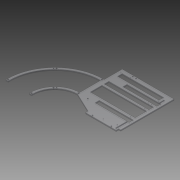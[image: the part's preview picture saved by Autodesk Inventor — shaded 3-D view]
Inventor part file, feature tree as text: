
AUTODESK INVENTOR PART (.ipt)
format: ipt  version: 2014 SP1 (Build 180222100, 222)  size: 401,920 bytes
history: native  units: in
note: dims shown in document units (in); Inventor stores cm internally (conversion verified against a paired STEP export)
features: extrude x18, sketch x18, reference x7
ambient origin geometry x8: Origin, YZ Plane, XZ Plane, XY Plane, X Axis, Y Axis, Z Axis, Center Point
bodies: Body1 (feature_tree)
feature tree (43):
  extrude  "Extrusion7"  Depth=1.0in
  extrude  "Extrusion8"  Depth=0.5in
  extrude  "Extrusion9"  Depth=5.25in
  extrude  "Extrusion10"  Depth=0.25in
  extrude  "Extrusion11"  Depth=7.625in
  extrude  "Extrusion13"  Depth=5.5in
  extrude  "Extrusion15"  Depth=12.125in
  extrude  "Extrusion16"  Depth=8.0in
  extrude  "Extrusion17"  Depth=2.75in
  extrude  "Extrusion18"  TaperAngle=90.0deg  [1 undecoded]
  extrude  "Extrusion19"  Depth=0.75in
  extrude  "Extrusion20"  Depth=10.5in
  extrude  "Extrusion21"  Depth=0.75in
  extrude  "Extrusion22"  Depth=10.5in
  extrude  "Extrusion23"  Depth=1.125in
  extrude  "Extrusion24"  Depth=0.5in
  extrude  "Extrusion25"  Depth=0.75in
  extrude  "Extrusion26"  Depth=1.0in TaperAngle=0.0deg
  sketch  "Sketch1"  dims[d2=0.5in d3=0.5in d10=0.5in d11=0.5in d13=0.5in d14=0.266in d15=0.266in d16=0.266in d18=0.266in d20=0.25in d21=0.266in d22=0.266in d23=0.266in d26=0.266in d30=0.266in d32=0.266in d66=1.0in]
  sketch  "Sketch7"  dims[d67=0.0in d72=0.5in]
  sketch  "Sketch8"  dims[d81=4.25in d82=5.25in]
  sketch  "Sketch9"  dims[d83=11.0in d84=0.25in]
  sketch  "Sketch10"  dims[d85=12.5in d86=7.625in]
  sketch  "Sketch13"  dims[d87=2.1762in d88=5.5in]
  sketch  "Sketch14"  dims[d89=0.25in d90=0.0in d91=12.125in]
  reference  "Reference4"
  sketch  "Sketch16"  dims[d92=1.0in d93=8.0in]
  sketch  "Sketch17"  dims[d94=0.5in d95=2.75in]
  sketch  "Sketch18"  dims[d98=0.25in d99=0.0in d100=90.0deg]
  sketch  "Sketch19"  dims[d101=0.875in d102=0.75in]
  sketch  "Sketch20"  dims[d103=1.125in d104=10.5in]
  reference  "Reference9"
  sketch  "Sketch21"  dims[d105=1.125in d106=0.75in]
  sketch  "Sketch22"  dims[d107=0.5in d108=10.5in]
  sketch  "Sketch23"  dims[d109=1.125in d110=1.125in]
  sketch  "Sketch24"  dims[d111=0.5in d112=0.5in]
  sketch  "Sketch25"  dims[d113=10.5in d114=0.75in]
  sketch  "Sketch26"  dims[d115=0.75in d116=1.0in d117=0.0in d118=11.125in d119=0.25in d120=11.5in d121=1.0in d122=0.0in d123=0.5in d124=1.375in d125=135.0deg d126=0.25in d127=0.0in d135=1.0in d136=13.25in d137=0.5in d138=1.0in d139=0.0in d146=0.25in d148=0.25in d149=0.375in d150=1.0in d151=0.0in d153=0.25in d154=0.0in d155=0.5in d156=0.5in d157=0.25in d158=0.0in d159=1.25in d160=0.25in d161=0.0in d162=0.266in d164=0.25in d165=2.75in d166=1.0in d167=0.0in d168=1.0in d169=0.0in d170=0.266in d171=0.266in d172=1.125in d173=1.375in d174=1.125in d176=0.125in d177=1.0in d178=0.0in d179=0.875in d180=0.25in d181=0.0in d182=0.875in d183=0.25in d184=0.0in d185=0.25in d186=0.0in d187=1.0in d188=0.0in d189=0.375in d190=0.125in d191=0.0in]
  reference  "Reference10"
  reference  "Reference11"
  reference  "Reference12"
  reference  "Reference13"
  reference  "Reference14"
note: 1 required parameter value undecoded (feature->parameter linkage not recoverable at this tier; creation-order binding heuristic only, values carry confidence <= 0.55)
